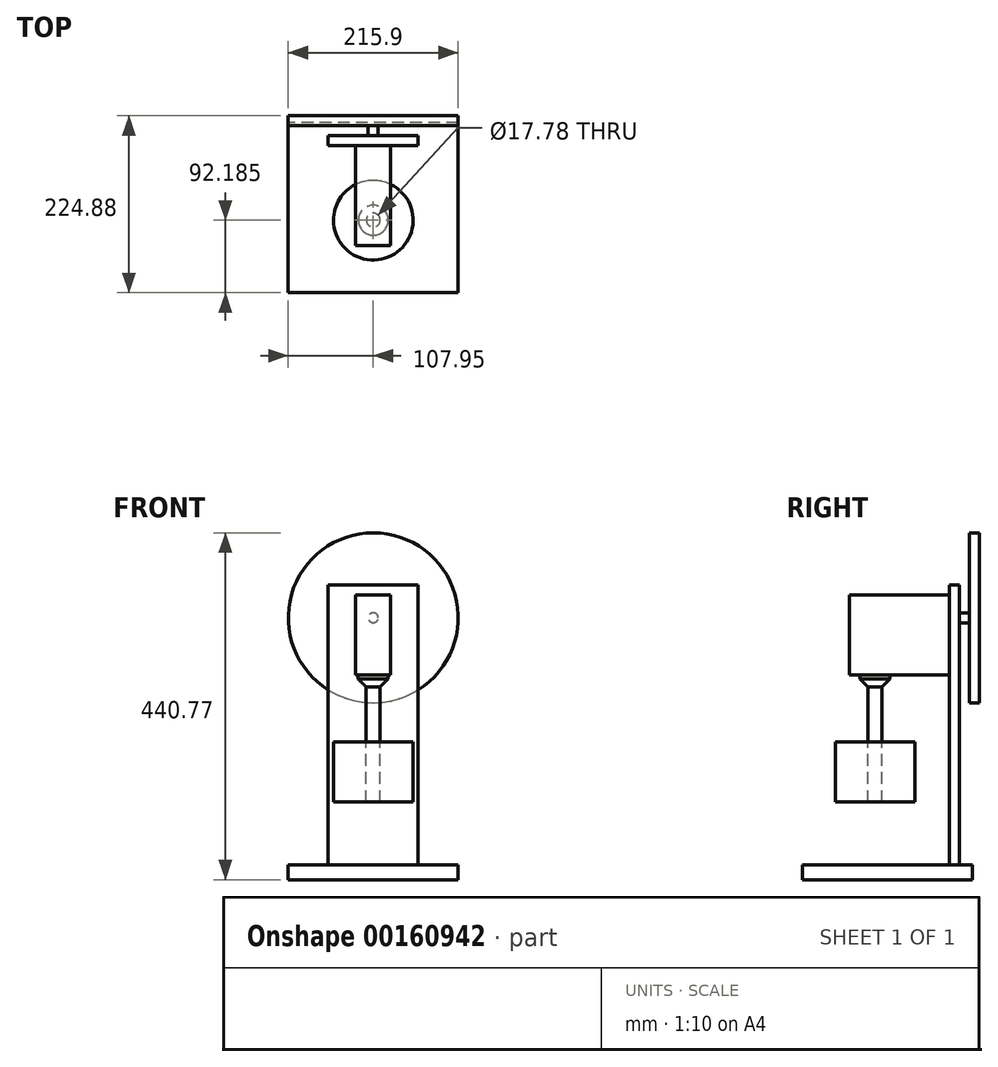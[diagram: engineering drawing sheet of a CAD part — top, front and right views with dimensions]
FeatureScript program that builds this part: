
annotation { "Feature Type Name" : "Feature", "Feature Type Description" : "" }
export const myFeature = defineFeature(function(context is Context, id is Id, definition is map)
    precondition{}
    {
        {
            var Q0;
            Q0=qCreatedBy(makeId("Top.planeOp"),FACE);
            var sketch = newSketch(context, id + "F0", { "sketchPlane" : qUnion([Q0])});
            skLineSegment(sketch, "E0.bottom", {"start": v(107.95, -107.95) * mm, "end": v(-107.95, -107.95) * mm});
            skLineSegment(sketch, "E0.top", {"start": v(107.95, 107.95) * mm, "end": v(-107.95, 107.95) * mm});
            skLineSegment(sketch, "E0.left", {"start": v(107.95, -107.95) * mm, "end": v(107.95, 107.95) * mm});
            skLineSegment(sketch, "E0.right", {"start": v(-107.95, -107.95) * mm, "end": v(-107.95, 107.95) * mm});
            skPoint(sketch, "E0.middle", {"position": v(0, 0) * mm});
            skSolve(sketch);
        }
        {
            var Q0;
            Q0=makeQuery(id+"F0.imprint","IMPRINT",FACE,{"disambiguationData":[TD([[makeQuery(id+"F0.imprint","IMPRINT",EDGE,{"derivedFrom":sQuery(id+"F0.wireOp",EDGE,"E0.bottom")}),-1.0]])]});
            extrude(context, id + "F1", {"entities" : qUnion([Q0]), "depth" : 19.05 * mm});
        }
        {
            var Q0;
            Q0=makeQuery(id+"F1.opExtrude","CAP_FACE",FACE,{"disambiguationData":[OSD([sQuery(id+"F0.wireOp",EDGE,"E0.bottom"),sQuery(id+"F0.wireOp",EDGE,"E0.top"),sQuery(id+"F0.wireOp",EDGE,"E0.left"),sQuery(id+"F0.wireOp",EDGE,"E0.right")])],"isStart":false});
            var sketch = newSketch(context, id + "F2", { "sketchPlane" : qUnion([Q0])});
            skSolve(sketch);
        }
        {
            var Q0;
            Q0=makeQuery(id+"F2.imprint","IMPRINT",FACE,{"disambiguationData":[TD([[makeQuery(id+"F2.imprint","IMPRINT",EDGE,{"derivedFrom":makeQuery(id+"F1.opExtrude","CAP_EDGE",EDGE,{"disambiguationData":[OSD([sQuery(id+"F0.wireOp",EDGE,"E0.bottom")])],"isStart":false})}),-1.0]])]});
            var sketch = newSketch(context, id + "F3", { "sketchPlane" : qUnion([Q0])});
            skLineSegment(sketch, "E1.bottom", {"start": v(-57.15, 91.53) * mm, "end": v(57.15, 91.53) * mm});
            skLineSegment(sketch, "E1.top", {"start": v(-57.15, 78.83) * mm, "end": v(57.15, 78.83) * mm});
            skLineSegment(sketch, "E1.left", {"start": v(-57.15, 91.53) * mm, "end": v(-57.15, 78.83) * mm});
            skLineSegment(sketch, "E1.right", {"start": v(57.15, 91.53) * mm, "end": v(57.15, 78.83) * mm});
            skLineSegment(sketch, "E2", {"start": v(-57.15, 91.53) * mm, "end": v(-107.95, 91.53) * mm, "construction": true});
            skLineSegment(sketch, "E3", {"start": v(57.15, 91.53) * mm, "end": v(107.95, 91.53) * mm, "construction": true});
            skSolve(sketch);
        }
        {
            var Q0;
            Q0 = qSketchRegion(id + "F3", true);
            extrude(context, id + "F4", {"entities" : qUnion([Q0]), "operationType" : NewBodyOperationType.ADD, "depth" : 355.6 * mm});
        }
        {
            var Q0;
            Q0=makeQuery(id+"F4.opExtrude","CAP_FACE",FACE,{"disambiguationData":[OSD([sQuery(id+"F3.wireOp",EDGE,"E1.bottom"),sQuery(id+"F3.wireOp",EDGE,"E1.top"),sQuery(id+"F3.wireOp",EDGE,"E1.left"),sQuery(id+"F3.wireOp",EDGE,"E1.right")])],"isStart":false});
            var sketch = newSketch(context, id + "F5", { "sketchPlane" : qUnion([Q0])});
            skLineSegment(sketch, "E4.bottom", {"start": v(-22.22, 78.83) * mm, "end": v(22.23, 78.83) * mm});
            skLineSegment(sketch, "E4.top", {"start": v(-22.22, -48.17) * mm, "end": v(22.23, -48.17) * mm});
            skLineSegment(sketch, "E4.left", {"start": v(-22.22, 78.83) * mm, "end": v(-22.22, -48.17) * mm});
            skLineSegment(sketch, "E4.right", {"start": v(22.23, 78.83) * mm, "end": v(22.23, -48.17) * mm});
            skSolve(sketch);
        }
        {
            var Q0;
            Q0 = qSketchRegion(id + "F5", true);
            extrude(context, id + "F6", {"entities" : qUnion([Q0]), "operationType" : NewBodyOperationType.ADD, "oppositeDirection" : true, "depth" : 114.3 * mm});
        }
        {
            var Q0;
            Q0=makeQuery(id+"F6.opExtrude","CAP_FACE",FACE,{"disambiguationData":[OSD([sQuery(id+"F5.wireOp",EDGE,"E4.bottom"),sQuery(id+"F5.wireOp",EDGE,"E4.top"),sQuery(id+"F5.wireOp",EDGE,"E4.left"),sQuery(id+"F5.wireOp",EDGE,"E4.right")])],"isStart":true});
            var sketch = newSketch(context, id + "F7", { "sketchPlane" : qUnion([Q0])});
            skLineSegment(sketch, "E5.0.0", {"start": v(-22.22, 78.83) * mm, "end": v(-22.22, -48.17) * mm});
            skLineSegment(sketch, "E5.0.1", {"start": v(-22.22, -48.17) * mm, "end": v(22.23, -48.17) * mm});
            skLineSegment(sketch, "E5.0.2", {"start": v(22.23, -48.17) * mm, "end": v(22.23, 78.83) * mm});
            skLineSegment(sketch, "E5.0.3", {"start": v(22.23, 78.83) * mm, "end": v(-22.22, 78.83) * mm});
            skSolve(sketch);
        }
        {
            var Q0;
            Q0 = qSketchRegion(id + "F7", true);
            extrude(context, id + "F8", {"entities" : qUnion([Q0]), "operationType" : NewBodyOperationType.REMOVE, "oppositeDirection" : true, "depth" : 12.7 * mm});
        }
        {
            var Q0;
            Q0=makeQuery(id+"F4.opExtrude","SWEPT_FACE",FACE,{"disambiguationData":[OSD([sQuery(id+"F3.wireOp",EDGE,"E1.bottom")])]});
            var sketch = newSketch(context, id + "F9", { "sketchPlane" : qUnion([Q0])});
            skCircle(sketch, "E6", {"center": v(0, 332.82) * mm, "radius": 6.35 * mm});
            skSolve(sketch);
        }
        {
            var Q0;
            Q0 = qSketchRegion(id + "F9", true);
            extrude(context, id + "F10", {"entities" : qUnion([Q0]), "operationType" : NewBodyOperationType.ADD, "depth" : 12.7 * mm});
        }
        {
            var Q0;
            Q0=makeQuery(id+"F10.opExtrude","CAP_FACE",FACE,{"disambiguationData":[OSD([sQuery(id+"F9.wireOp",EDGE,"E6")])],"isStart":false});
            var sketch = newSketch(context, id + "F11", { "sketchPlane" : qUnion([Q0])});
            skCircle(sketch, "E7", {"center": v(0, 332.82) * mm, "radius": 107.95 * mm});
            skSolve(sketch);
        }
        {
            var Q0;
            Q0 = qSketchRegion(id + "F11", true);
            extrude(context, id + "F12", {"entities" : qUnion([Q0]), "operationType" : NewBodyOperationType.ADD, "depth" : 12.7 * mm});
        }
        {
            var Q0;
            Q0=makeQuery(id+"F6.opExtrude","CAP_FACE",FACE,{"disambiguationData":[OSD([sQuery(id+"F5.wireOp",EDGE,"E4.bottom"),sQuery(id+"F5.wireOp",EDGE,"E4.top"),sQuery(id+"F5.wireOp",EDGE,"E4.left"),sQuery(id+"F5.wireOp",EDGE,"E4.right")])],"isStart":false});
            var sketch = newSketch(context, id + "F13", { "sketchPlane" : qUnion([Q0])});
            skCircle(sketch, "E8", {"center": v(0, 15.76) * mm, "radius": 19.05 * mm});
            skSolve(sketch);
        }
        {
            var Q0;
            Q0 = qSketchRegion(id + "F13", true);
            extrude(context, id + "F14", {"entities" : qUnion([Q0]), "operationType" : NewBodyOperationType.ADD, "depth" : 15.5 * mm});
        }
        {
            var Q0;
            Q0=makeQuery(id+"F14.opExtrude","CAP_EDGE",EDGE,{"disambiguationData":[OSD([sQuery(id+"F13.wireOp",EDGE,"E8")])],"isStart":false});
            chamfer(context, id + "F15", {"entities" : qUnion([Q0]), "width" : 10.16 * mm, "tangentPropagation" : true});
        }
        {
            var Q0;
            Q0=makeQuery(id+"F14.opExtrude","CAP_FACE",FACE,{"disambiguationData":[OSD([sQuery(id+"F13.wireOp",EDGE,"E8")])],"isStart":false});
            var sketch = newSketch(context, id + "F16", { "sketchPlane" : qUnion([Q0])});
            skCircle(sketch, "E9.0.0", {"center": v(0, 15.76) * mm, "radius": 8.9 * mm});
            skSolve(sketch);
        }
        {
            var Q0;
            Q0 = qSketchRegion(id + "F16", true);
            extrude(context, id + "F17", {"entities" : qUnion([Q0]), "operationType" : NewBodyOperationType.ADD, "depth" : 44.45 * mm});
        }
        {
            var Q0;
            Q0=makeQuery(id+"F17.opExtrude","CAP_FACE",FACE,{"disambiguationData":[OSD([sQuery(id+"F16.wireOp",EDGE,"E9.0.0")])],"isStart":false});
            extrude(context, id + "F18", {"entities" : qUnion([Q0]), "operationType" : NewBodyOperationType.ADD, "depth" : 25.4 * mm});
        }
        {
            var Q0;
            Q0=makeQuery(id+"F18.opExtrude","CAP_FACE",FACE,{"disambiguationData":[OSD([sQuery(id+"F16.wireOp",EDGE,"E9.0.0")])],"isStart":false});
            var sketch = newSketch(context, id + "F19", { "sketchPlane" : qUnion([Q0])});
            skCircle(sketch, "E10", {"center": v(0, 15.76) * mm, "radius": 50.59 * mm});
            skSolve(sketch);
        }
        {
            var Q0;
            Q0=makeQuery(id+"F19.imprint","IMPRINT",FACE,{"disambiguationData":[TD([[makeQuery(id+"F19.imprint","IMPRINT",EDGE,{"derivedFrom":sQuery(id+"F19.wireOp",EDGE,"E10")}),1.0]])]});
            extrude(context, id + "F20", {"entities" : qUnion([Q0]), "depth" : 76.2 * mm});
        }
    });
